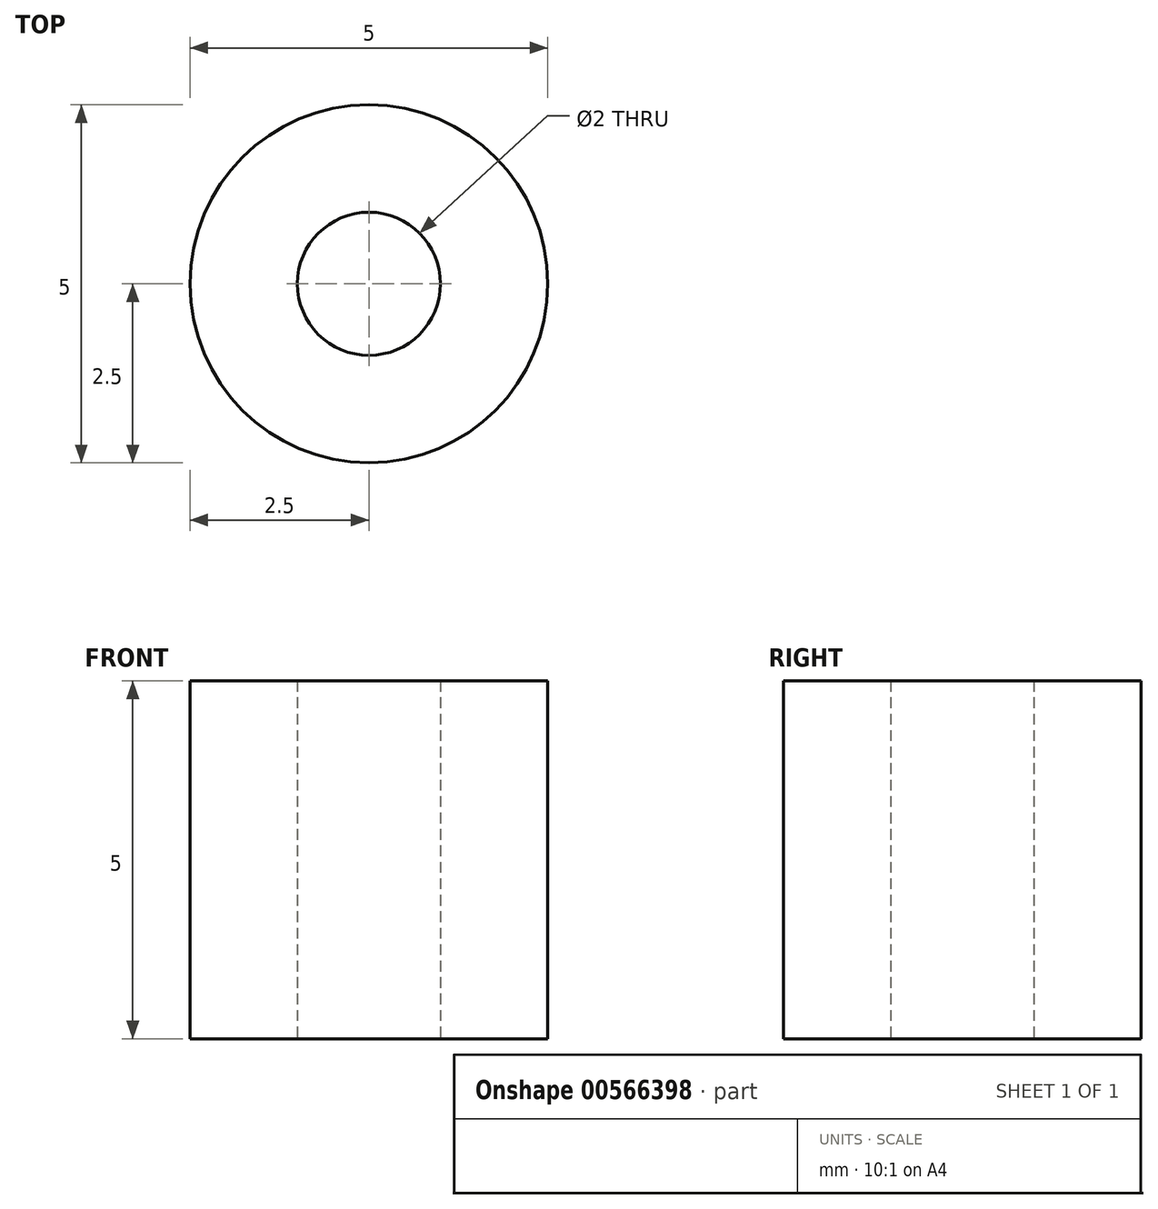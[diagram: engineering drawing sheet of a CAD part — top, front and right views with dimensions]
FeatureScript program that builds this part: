
annotation { "Feature Type Name" : "Feature", "Feature Type Description" : "" }
export const myFeature = defineFeature(function(context is Context, id is Id, definition is map)
    precondition{}
    {
        {
            var Q0;
            Q0=qCreatedBy(makeId("Top.planeOp"),FACE);
            var sketch = newSketch(context, id + "F0", { "sketchPlane" : qUnion([Q0])});
            skCircle(sketch, "E0", {"center": v(0, 0) * mm, "radius": 1 * mm});
            skCircle(sketch, "E1", {"center": v(0, 0) * mm, "radius": 2.5 * mm});
            skSolve(sketch);
        }
        {
            var Q0;
            Q0=qSketchRegion(id+"F0",true);
            extrude(context, id + "F1", {"entities" : qUnion([Q0]), "depth" : 5 * mm, "offsetDistance" : 25 * mm});
        }
    });
